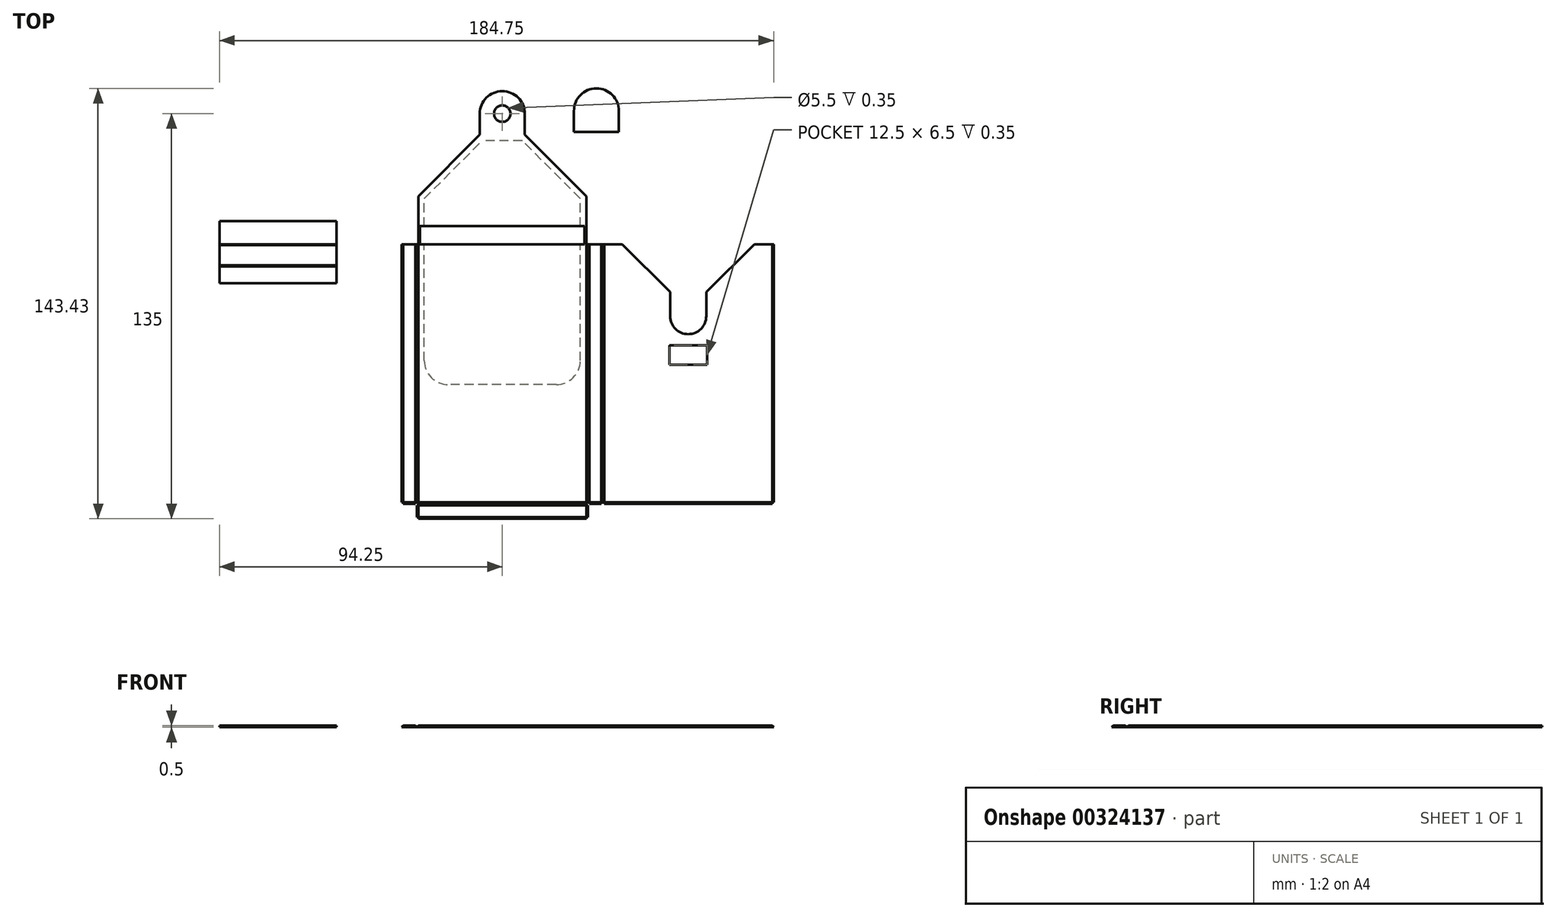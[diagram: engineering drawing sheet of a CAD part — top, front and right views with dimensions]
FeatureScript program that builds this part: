
annotation { "Feature Type Name" : "Feature", "Feature Type Description" : "" }
export const myFeature = defineFeature(function(context is Context, id is Id, definition is map)
    precondition{}
    {
        {
            var Q0;
            Q0=qCreatedBy(makeId("Top.planeOp"),FACE);
            var sketch = newSketch(context, id + "F0", { "sketchPlane" : qUnion([Q0])});
            skLineSegment(sketch, "E0.bottom", {"start": v(0, 0) * mm, "end": v(56, 0) * mm});
            skLineSegment(sketch, "E0.top", {"start": v(0, -86) * mm, "end": v(56, -86) * mm});
            skLineSegment(sketch, "E0.left", {"start": v(0, 0) * mm, "end": v(0, -86) * mm});
            skLineSegment(sketch, "E0.right", {"start": v(56, 0) * mm, "end": v(56, -86) * mm});
            skLineSegment(sketch, "E1.bottom", {"start": v(56, 0) * mm, "end": v(56.5, 0) * mm});
            skLineSegment(sketch, "E1.top", {"start": v(56, -86) * mm, "end": v(56.5, -86) * mm});
            skLineSegment(sketch, "E1.right", {"start": v(56.5, 0) * mm, "end": v(56.5, -86) * mm});
            skLineSegment(sketch, "E2.bottom", {"start": v(56.5, 0) * mm, "end": v(57, 0) * mm});
            skLineSegment(sketch, "E2.top", {"start": v(56.5, -86) * mm, "end": v(57, -86) * mm});
            skLineSegment(sketch, "E2.right", {"start": v(57, 0) * mm, "end": v(57, -86) * mm});
            skLineSegment(sketch, "E3.bottom", {"start": v(57, 0) * mm, "end": v(61, 0) * mm});
            skLineSegment(sketch, "E3.top", {"start": v(57, -86) * mm, "end": v(61, -86) * mm});
            skLineSegment(sketch, "E3.right", {"start": v(61, 0) * mm, "end": v(61, -86) * mm});
            skLineSegment(sketch, "E4.bottom", {"start": v(61, 0) * mm, "end": v(61.5, 0) * mm});
            skLineSegment(sketch, "E4.top", {"start": v(61, -86) * mm, "end": v(61.5, -86) * mm});
            skLineSegment(sketch, "E4.right", {"start": v(61.5, 0) * mm, "end": v(61.5, -86) * mm});
            skLineSegment(sketch, "E5.bottom", {"start": v(61.5, 0) * mm, "end": v(62, 0) * mm});
            skLineSegment(sketch, "E5.top", {"start": v(61.5, -86) * mm, "end": v(62, -86) * mm});
            skLineSegment(sketch, "E5.right", {"start": v(62, 0) * mm, "end": v(62, -86) * mm});
            skLineSegment(sketch, "E6.bottom", {"start": v(62, 0) * mm, "end": v(84, 0) * mm});
            skLineSegment(sketch, "E6.top", {"start": v(62, -86) * mm, "end": v(118, -86) * mm});
            skLineSegment(sketch, "E6.right", {"start": v(118, 0) * mm, "end": v(118, -86) * mm});
            skLineSegment(sketch, "E7", {"start": v(28, 0) * mm, "end": v(28, -86) * mm, "construction": true});
            skLineSegment(sketch, "E8.MirrorCS", {"start": v(-0.5, 0) * mm, "end": v(-0.5, -86) * mm});
            skLineSegment(sketch, "E9.MirrorCS", {"start": v(-1, 0) * mm, "end": v(-1, -86) * mm});
            skLineSegment(sketch, "E10.MirrorCS", {"start": v(-5, 0) * mm, "end": v(-5, -86) * mm});
            skLineSegment(sketch, "E11.MirrorCS", {"start": v(-1, 0) * mm, "end": v(-5, 0) * mm});
            skLineSegment(sketch, "E12.MirrorCS", {"start": v(0, 0) * mm, "end": v(-0.5, 0) * mm});
            skLineSegment(sketch, "E13.MirrorCS", {"start": v(-0.5, 0) * mm, "end": v(-1, 0) * mm});
            skLineSegment(sketch, "E14.MirrorCS", {"start": v(-1, -86) * mm, "end": v(-5, -86) * mm});
            skLineSegment(sketch, "E15.MirrorCS", {"start": v(0, -86) * mm, "end": v(-0.5, -86) * mm});
            skLineSegment(sketch, "E16.MirrorCS", {"start": v(-0.5, -86) * mm, "end": v(-1, -86) * mm});
            skLineSegment(sketch, "E17.MirrorCS", {"start": v(-5.5, 0) * mm, "end": v(-5.5, -86) * mm});
            skLineSegment(sketch, "E18.MirrorCS", {"start": v(-5, 0) * mm, "end": v(-5.5, 0) * mm});
            skLineSegment(sketch, "E19.MirrorCS", {"start": v(-5, -86) * mm, "end": v(-5.5, -86) * mm});
            skLineSegment(sketch, "E20.bottom", {"start": v(118, 0) * mm, "end": v(118.5, 0) * mm});
            skLineSegment(sketch, "E20.top", {"start": v(118, -86) * mm, "end": v(118.5, -86) * mm});
            skLineSegment(sketch, "E20.right", {"start": v(118.5, 0) * mm, "end": v(118.5, -86) * mm});
            skLineSegment(sketch, "E21.top", {"start": v(0, -86.5) * mm, "end": v(56, -86.5) * mm});
            skLineSegment(sketch, "E21.left", {"start": v(0, -86) * mm, "end": v(0, -86.5) * mm});
            skLineSegment(sketch, "E21.right", {"start": v(56, -86) * mm, "end": v(56, -86.5) * mm});
            skLineSegment(sketch, "E22.bottom", {"start": v(56, -86.5) * mm, "end": v(0, -86.5) * mm});
            skLineSegment(sketch, "E22.top", {"start": v(56, -87) * mm, "end": v(0, -87) * mm});
            skLineSegment(sketch, "E22.left", {"start": v(56, -86.5) * mm, "end": v(56, -87) * mm});
            skLineSegment(sketch, "E22.right", {"start": v(0, -86.5) * mm, "end": v(0, -87) * mm});
            skLineSegment(sketch, "E23.bottom", {"start": v(0, -87) * mm, "end": v(56, -87) * mm});
            skLineSegment(sketch, "E23.top", {"start": v(0, -91) * mm, "end": v(56, -91) * mm});
            skLineSegment(sketch, "E23.left", {"start": v(0, -87) * mm, "end": v(0, -91) * mm});
            skLineSegment(sketch, "E23.right", {"start": v(56, -87) * mm, "end": v(56, -91) * mm});
            skLineSegment(sketch, "E24.bottom", {"start": v(56, -91) * mm, "end": v(0, -91) * mm});
            skLineSegment(sketch, "E24.top", {"start": v(56, -91.5) * mm, "end": v(0, -91.5) * mm});
            skLineSegment(sketch, "E24.left", {"start": v(56, -91) * mm, "end": v(56, -91.5) * mm});
            skLineSegment(sketch, "E24.right", {"start": v(0, -91) * mm, "end": v(0, -91.5) * mm});
            skLineSegment(sketch, "E25.bottom", {"start": v(-5, -86) * mm, "end": v(-1, -86) * mm});
            skLineSegment(sketch, "E25.top", {"start": v(-5, -86.5) * mm, "end": v(-1, -86.5) * mm});
            skLineSegment(sketch, "E25.left", {"start": v(-5, -86) * mm, "end": v(-5, -86.5) * mm});
            skLineSegment(sketch, "E25.right", {"start": v(-1, -86) * mm, "end": v(-1, -86.5) * mm});
            skLineSegment(sketch, "E26.bottom", {"start": v(0, -87) * mm, "end": v(-0.5, -87) * mm});
            skLineSegment(sketch, "E26.top", {"start": v(0, -91) * mm, "end": v(-0.5, -91) * mm});
            skLineSegment(sketch, "E26.right", {"start": v(-0.5, -87) * mm, "end": v(-0.5, -91) * mm});
            skLineSegment(sketch, "E27.bottom", {"start": v(56, -87) * mm, "end": v(56.5, -87) * mm});
            skLineSegment(sketch, "E27.top", {"start": v(56, -91) * mm, "end": v(56.5, -91) * mm});
            skLineSegment(sketch, "E27.right", {"start": v(56.5, -87) * mm, "end": v(56.5, -91) * mm});
            skLineSegment(sketch, "E28.top", {"start": v(57, -86.5) * mm, "end": v(61, -86.5) * mm});
            skLineSegment(sketch, "E28.left", {"start": v(57, -86) * mm, "end": v(57, -86.5) * mm});
            skLineSegment(sketch, "E28.right", {"start": v(61, -86) * mm, "end": v(61, -86.5) * mm});
            skLineSegment(sketch, "E29.top", {"start": v(62, -86.5) * mm, "end": v(118, -86.5) * mm});
            skLineSegment(sketch, "E29.left", {"start": v(62, -86) * mm, "end": v(62, -86.5) * mm});
            skLineSegment(sketch, "E29.right", {"start": v(118, -86) * mm, "end": v(118, -86.5) * mm});
            skLineSegment(sketch, "E30.top", {"start": v(0, 8) * mm, "end": v(56, 8) * mm});
            skLineSegment(sketch, "E30.left", {"start": v(0, 0) * mm, "end": v(0, 8) * mm});
            skLineSegment(sketch, "E30.right", {"start": v(56, 0) * mm, "end": v(56, 8) * mm});
            skLineSegment(sketch, "E31.top", {"start": v(0, 51) * mm, "end": v(56, 51) * mm});
            skLineSegment(sketch, "E31.left", {"start": v(0, 8) * mm, "end": v(0, 51) * mm});
            skLineSegment(sketch, "E31.right", {"start": v(56, 8) * mm, "end": v(56, 51) * mm});
            skPoint(sketch, "E32.visualSharp", {"position": v(0, 51) * mm});
            skLineSegment(sketch, "E32.filletArc", {"start": v(0, 51) * mm, "end": v(0, 51) * mm});
            skPoint(sketch, "E33.visualSharp", {"position": v(56, 51) * mm});
            skLineSegment(sketch, "E33.filletArc", {"start": v(56, 51) * mm, "end": v(56, 51) * mm});
            skLineSegment(sketch, "E34.top", {"start": v(96, -30) * mm, "end": v(84, -30) * mm});
            skLineSegment(sketch, "E34.left", {"start": v(96, 0) * mm, "end": v(96, -30) * mm});
            skLineSegment(sketch, "E34.right", {"start": v(84, 0) * mm, "end": v(84, -30) * mm});
            skPoint(sketch, "E34.middle", {"position": v(90, -15) * mm});
            skPoint(sketch, "E34.middle.positionSnap0", {"position": v(90, 0) * mm});
            skPoint(sketch, "E34.centerSnap0", {"position": v(90, 0) * mm});
            skLineSegment(sketch, "E35.trimOffspring", {"start": v(96, 0) * mm, "end": v(118, 0) * mm});
            skSolve(sketch);
        }
        {
            var Q0;
            Q0 = qSketchRegion(id + "F0", true);
            extrude(context, id + "F1", {"entities" : qUnion([Q0]), "depth" : 0.5 * mm});
        }
        {
            var Q0;
            Q0=makeQuery(id+"F1.opExtrude","CAP_EDGE",EDGE,{"disambiguationData":[OSD([sQuery(id+"F0.wireOp",EDGE,"E17.MirrorCS")])],"isStart":false});
            var Q1;
            Q1=makeQuery(id+"F1.opExtrude","CAP_EDGE",EDGE,{"disambiguationData":[OSD([sQuery(id+"F0.wireOp",EDGE,"E25.top")])],"isStart":false});
            var Q2;
            Q2=makeQuery(id+"F1.opExtrude","CAP_EDGE",EDGE,{"disambiguationData":[OSD([sQuery(id+"F0.wireOp",EDGE,"E26.right")])],"isStart":false});
            var Q3;
            Q3=makeQuery(id+"F1.opExtrude","CAP_EDGE",EDGE,{"disambiguationData":[OSD([sQuery(id+"F0.wireOp",EDGE,"E24.top")])],"isStart":false});
            var Q4;
            Q4=makeQuery(id+"F1.opExtrude","CAP_EDGE",EDGE,{"disambiguationData":[OSD([sQuery(id+"F0.wireOp",EDGE,"E27.right")])],"isStart":false});
            var Q5;
            Q5=makeQuery(id+"F1.opExtrude","CAP_EDGE",EDGE,{"disambiguationData":[OSD([sQuery(id+"F0.wireOp",EDGE,"E28.top")])],"isStart":false});
            var Q6;
            Q6=makeQuery(id+"F1.opExtrude","CAP_EDGE",EDGE,{"disambiguationData":[OSD([sQuery(id+"F0.wireOp",EDGE,"E29.top")])],"isStart":false});
            var Q7;
            Q7=makeQuery(id+"F1.opExtrude","CAP_EDGE",EDGE,{"disambiguationData":[OSD([sQuery(id+"F0.wireOp",EDGE,"E20.right")])],"isStart":false});
            chamfer(context, id + "F2", {"entities" : qUnion([Q0, Q1, Q2, Q3, Q4, Q5, Q6, Q7]), "chamferType" : ChamferType.OFFSET_ANGLE, "width" : 0.5 * mm, "oppositeDirection" : false, "angle" : 45 * degree, "tangentPropagation" : true});
        }
        {
            var Q0;
            Q0=makeQuery(id+"F1.opExtrude","SWEPT_FACE",FACE,{"disambiguationData":[OSD([sQuery(id+"F0.wireOp",EDGE,"E15.MirrorCS"),sQuery(id+"F0.wireOp",EDGE,"E16.MirrorCS")])]});
            var sketch = newSketch(context, id + "F3", { "sketchPlane" : qUnion([Q0])});
            skLineSegment(sketch, "E36", {"start": v(-1, 0.5) * mm, "end": v(0, 0.5) * mm});
            skLineSegment(sketch, "E37", {"start": v(0, 0.5) * mm, "end": v(-0.35, 0.15) * mm});
            skLineSegment(sketch, "E38", {"start": v(-0.35, 0.15) * mm, "end": v(-0.65, 0.15) * mm});
            skLineSegment(sketch, "E39", {"start": v(-0.65, 0.15) * mm, "end": v(-1, 0.5) * mm});
            skLineSegment(sketch, "E40", {"start": v(56, 0.5) * mm, "end": v(57, 0.5) * mm});
            skLineSegment(sketch, "E41", {"start": v(57, 0.5) * mm, "end": v(56.65, 0.15) * mm});
            skLineSegment(sketch, "E42", {"start": v(56.65, 0.15) * mm, "end": v(56.35, 0.15) * mm});
            skLineSegment(sketch, "E43", {"start": v(56.35, 0.15) * mm, "end": v(56, 0.5) * mm});
            skLineSegment(sketch, "E44", {"start": v(61, 0.5) * mm, "end": v(62, 0.5) * mm});
            skLineSegment(sketch, "E45", {"start": v(62, 0.5) * mm, "end": v(61.65, 0.15) * mm});
            skLineSegment(sketch, "E46", {"start": v(61.65, 0.15) * mm, "end": v(61.35, 0.15) * mm});
            skLineSegment(sketch, "E47", {"start": v(61.35, 0.15) * mm, "end": v(61, 0.5) * mm});
            skSolve(sketch);
        }
        {
            var Q0;
            Q0 = qSketchRegion(id + "F3", true);
            extrude(context, id + "F4", {"entities" : qUnion([Q0]), "operationType" : NewBodyOperationType.REMOVE, "endBound" : BoundingType.UP_TO_NEXT, "oppositeDirection" : true, "depth" : 25 * mm});
        }
        {
            var Q0;
            {var subQ0=sQuery(id+"F0.wireOp",EDGE,"E26.top");var subQ1=sQuery(id+"F0.wireOp",EDGE,"E26.bottom");var subQ2=sQuery(id+"F0.wireOp",EDGE,"E24.left");var subQ3=sQuery(id+"F0.wireOp",EDGE,"E22.right");var subQ4=sQuery(id+"F0.wireOp",EDGE,"E21.left");var subQ5=sQuery(id+"F0.wireOp",EDGE,"E22.left");var subQ6=sQuery(id+"F0.wireOp",EDGE,"E21.right");var subQ7=sQuery(id+"F0.wireOp",EDGE,"E26.right");var subQ8=sQuery(id+"F0.wireOp",EDGE,"E6.bottom");var subQ9=sQuery(id+"F0.wireOp",EDGE,"E5.bottom");var subQ10=sQuery(id+"F0.wireOp",EDGE,"E4.bottom");var subQ11=sQuery(id+"F0.wireOp",EDGE,"E3.bottom");var subQ12=sQuery(id+"F0.wireOp",EDGE,"E2.bottom");var subQ13=sQuery(id+"F0.wireOp",EDGE,"E1.bottom");var subQ14=sQuery(id+"F0.wireOp",EDGE,"E2.top");var subQ15=sQuery(id+"F0.wireOp",EDGE,"E1.top");var subQ16=sQuery(id+"F0.wireOp",EDGE,"E24.right");var subQ17=sQuery(id+"F0.wireOp",EDGE,"E18.MirrorCS");var subQ18=sQuery(id+"F0.wireOp",EDGE,"E13.MirrorCS");var subQ19=sQuery(id+"F0.wireOp",EDGE,"E12.MirrorCS");var subQ20=sQuery(id+"F0.wireOp",EDGE,"E11.MirrorCS");var subQ21=sQuery(id+"F0.wireOp",EDGE,"E16.MirrorCS");var subQ22=sQuery(id+"F0.wireOp",EDGE,"E15.MirrorCS");var subQ23=sQuery(id+"F0.wireOp",EDGE,"E27.bottom");var subQ24=sQuery(id+"F0.wireOp",EDGE,"E27.top");var subQ25=sQuery(id+"F0.wireOp",EDGE,"E31.left");var subQ26=sQuery(id+"F0.wireOp",EDGE,"E30.left");var subQ27=sQuery(id+"F0.wireOp",EDGE,"E31.right");var subQ28=sQuery(id+"F0.wireOp",EDGE,"E30.right");var subQ29=sQuery(id+"F0.wireOp",EDGE,"E31.top");var subQ30=sQuery(id+"F0.wireOp",EDGE,"E24.top");var subQ31=sQuery(id+"F0.wireOp",EDGE,"E27.right");Q0=makeQuery(id+"F4.boolean.opBoolean","SPLIT",FACE,{"disambiguationData":[TD([makeQuery(id+"F1.opExtrude","SWEPT_FACE",FACE,{"disambiguationData":[OSD([subQ2])]})])],"derivedFrom":makeQuery(id+"F1.opExtrude","CAP_FACE",FACE,{"disambiguationData":[OSD([subQ13,subQ15,subQ12,subQ14,subQ11,subQ10,sQuery(id+"F0.wireOp",EDGE,"E4.top"),subQ9,sQuery(id+"F0.wireOp",EDGE,"E5.top"),subQ8,subQ20,subQ19,subQ18,subQ22,subQ21,sQuery(id+"F0.wireOp",EDGE,"E17.MirrorCS"),subQ17,sQuery(id+"F0.wireOp",EDGE,"E19.MirrorCS"),sQuery(id+"F0.wireOp",EDGE,"E20.bottom"),sQuery(id+"F0.wireOp",EDGE,"E20.top"),sQuery(id+"F0.wireOp",EDGE,"E20.right"),subQ4,subQ6,subQ5,subQ3,subQ30,subQ2,subQ16,sQuery(id+"F0.wireOp",EDGE,"E25.top"),sQuery(id+"F0.wireOp",EDGE,"E25.left"),sQuery(id+"F0.wireOp",EDGE,"E25.right"),subQ1,subQ0,subQ7,subQ23,subQ24,subQ31,sQuery(id+"F0.wireOp",EDGE,"E28.top"),sQuery(id+"F0.wireOp",EDGE,"E28.left"),sQuery(id+"F0.wireOp",EDGE,"E28.right"),sQuery(id+"F0.wireOp",EDGE,"E29.top"),sQuery(id+"F0.wireOp",EDGE,"E29.left"),sQuery(id+"F0.wireOp",EDGE,"E29.right"),subQ26,subQ28,subQ29,subQ25,subQ27,sQuery(id+"F0.wireOp",EDGE,"E34.top"),sQuery(id+"F0.wireOp",EDGE,"E34.left"),sQuery(id+"F0.wireOp",EDGE,"E34.right"),sQuery(id+"F0.wireOp",EDGE,"E35.trimOffspring")])],"isStart":false})});}
            var sketch = newSketch(context, id + "F5", { "sketchPlane" : qUnion([Q0])});
            skLineSegment(sketch, "E48", {"start": v(28, 51) * mm, "end": v(28, 0) * mm, "construction": true});
            skLineSegment(sketch, "E49", {"start": v(22, 51) * mm, "end": v(28, 51) * mm});
            skLineSegment(sketch, "E50", {"start": v(20.5, 43.5) * mm, "end": v(20.5, 36.5) * mm});
            skLineSegment(sketch, "E51", {"start": v(20.5, 36.5) * mm, "end": v(0, 16) * mm});
            skLineSegment(sketch, "E52", {"start": v(0, 16) * mm, "end": v(0, 51) * mm});
            skLineSegment(sketch, "E53", {"start": v(0, 51) * mm, "end": v(22, 51) * mm});
            skLineSegment(sketch, "E54.MirrorCS", {"start": v(56, 51) * mm, "end": v(34, 51) * mm});
            skLineSegment(sketch, "E55.MirrorCS", {"start": v(35.5, 43.5) * mm, "end": v(35.5, 36.5) * mm});
            skLineSegment(sketch, "E56.MirrorCS", {"start": v(35.5, 36.5) * mm, "end": v(56, 16) * mm});
            skLineSegment(sketch, "E57.MirrorCS", {"start": v(56, 16) * mm, "end": v(56, 51) * mm});
            skArc(sketch, "E58", {"start": v(35.5, 43.5) * mm, "mid": v(28, 51) * mm, "end": v(20.5, 43.5) * mm});
            skLineSegment(sketch, "E59", {"start": v(28, 51) * mm, "end": v(34, 51) * mm});
            skSolve(sketch);
        }
        {
            var Q0;
            Q0 = qSketchRegion(id + "F5", true);
            extrude(context, id + "F6", {"entities" : qUnion([Q0]), "operationType" : NewBodyOperationType.REMOVE, "oppositeDirection" : true, "depth" : 25 * mm});
        }
        {
            var Q0;
            {var subQ0=sQuery(id+"F0.wireOp",EDGE,"E26.top");var subQ1=sQuery(id+"F0.wireOp",EDGE,"E26.bottom");var subQ2=sQuery(id+"F0.wireOp",EDGE,"E24.left");var subQ3=sQuery(id+"F0.wireOp",EDGE,"E22.right");var subQ4=sQuery(id+"F0.wireOp",EDGE,"E21.left");var subQ5=sQuery(id+"F0.wireOp",EDGE,"E22.left");var subQ6=sQuery(id+"F0.wireOp",EDGE,"E21.right");var subQ7=sQuery(id+"F0.wireOp",EDGE,"E26.right");var subQ8=sQuery(id+"F0.wireOp",EDGE,"E6.bottom");var subQ9=sQuery(id+"F0.wireOp",EDGE,"E5.bottom");var subQ10=sQuery(id+"F0.wireOp",EDGE,"E4.bottom");var subQ11=sQuery(id+"F0.wireOp",EDGE,"E3.bottom");var subQ12=sQuery(id+"F0.wireOp",EDGE,"E2.bottom");var subQ13=sQuery(id+"F0.wireOp",EDGE,"E1.bottom");var subQ14=sQuery(id+"F0.wireOp",EDGE,"E2.top");var subQ15=sQuery(id+"F0.wireOp",EDGE,"E1.top");var subQ16=sQuery(id+"F0.wireOp",EDGE,"E24.right");var subQ17=sQuery(id+"F0.wireOp",EDGE,"E18.MirrorCS");var subQ18=sQuery(id+"F0.wireOp",EDGE,"E13.MirrorCS");var subQ19=sQuery(id+"F0.wireOp",EDGE,"E12.MirrorCS");var subQ20=sQuery(id+"F0.wireOp",EDGE,"E11.MirrorCS");var subQ21=sQuery(id+"F0.wireOp",EDGE,"E16.MirrorCS");var subQ22=sQuery(id+"F0.wireOp",EDGE,"E15.MirrorCS");var subQ23=sQuery(id+"F0.wireOp",EDGE,"E27.bottom");var subQ24=sQuery(id+"F0.wireOp",EDGE,"E27.top");var subQ25=sQuery(id+"F0.wireOp",EDGE,"E31.left");var subQ26=sQuery(id+"F0.wireOp",EDGE,"E30.left");var subQ27=sQuery(id+"F0.wireOp",EDGE,"E31.right");var subQ28=sQuery(id+"F0.wireOp",EDGE,"E30.right");var subQ29=sQuery(id+"F0.wireOp",EDGE,"E31.top");var subQ30=sQuery(id+"F0.wireOp",EDGE,"E24.top");var subQ31=sQuery(id+"F0.wireOp",EDGE,"E27.right");Q0=makeQuery(id+"F4.boolean.opBoolean","SPLIT",FACE,{"disambiguationData":[TD([makeQuery(id+"F1.opExtrude","SWEPT_FACE",FACE,{"disambiguationData":[OSD([subQ2])]})])],"derivedFrom":makeQuery(id+"F1.opExtrude","CAP_FACE",FACE,{"disambiguationData":[OSD([subQ13,subQ15,subQ12,subQ14,subQ11,subQ10,sQuery(id+"F0.wireOp",EDGE,"E4.top"),subQ9,sQuery(id+"F0.wireOp",EDGE,"E5.top"),subQ8,subQ20,subQ19,subQ18,subQ22,subQ21,sQuery(id+"F0.wireOp",EDGE,"E17.MirrorCS"),subQ17,sQuery(id+"F0.wireOp",EDGE,"E19.MirrorCS"),sQuery(id+"F0.wireOp",EDGE,"E20.bottom"),sQuery(id+"F0.wireOp",EDGE,"E20.top"),sQuery(id+"F0.wireOp",EDGE,"E20.right"),subQ4,subQ6,subQ5,subQ3,subQ30,subQ2,subQ16,sQuery(id+"F0.wireOp",EDGE,"E25.top"),sQuery(id+"F0.wireOp",EDGE,"E25.left"),sQuery(id+"F0.wireOp",EDGE,"E25.right"),subQ1,subQ0,subQ7,subQ23,subQ24,subQ31,sQuery(id+"F0.wireOp",EDGE,"E28.top"),sQuery(id+"F0.wireOp",EDGE,"E28.left"),sQuery(id+"F0.wireOp",EDGE,"E28.right"),sQuery(id+"F0.wireOp",EDGE,"E29.top"),sQuery(id+"F0.wireOp",EDGE,"E29.left"),sQuery(id+"F0.wireOp",EDGE,"E29.right"),subQ26,subQ28,subQ29,subQ25,subQ27,sQuery(id+"F0.wireOp",EDGE,"E34.top"),sQuery(id+"F0.wireOp",EDGE,"E34.left"),sQuery(id+"F0.wireOp",EDGE,"E34.right"),sQuery(id+"F0.wireOp",EDGE,"E35.trimOffspring")])],"isStart":false})});}
            var sketch = newSketch(context, id + "F7", { "sketchPlane" : qUnion([Q0])});
            skCircle(sketch, "E60", {"center": v(28, 43.5) * mm, "radius": 2.75 * mm});
            skPoint(sketch, "E60.centerSnap0", {"position": v(28, 54) * mm});
            skSolve(sketch);
        }
        {
            var Q0;
            Q0 = qSketchRegion(id + "F7", true);
            extrude(context, id + "F8", {"entities" : qUnion([Q0]), "operationType" : NewBodyOperationType.REMOVE, "oppositeDirection" : true, "depth" : 0.35 * mm});
        }
        {
            var Q0;
            {var subQ0=sQuery(id+"F0.wireOp",EDGE,"E20.right");var subQ1=sQuery(id+"F0.wireOp",EDGE,"E20.top");var subQ2=sQuery(id+"F0.wireOp",EDGE,"E34.left");var subQ3=sQuery(id+"F0.wireOp",EDGE,"E29.left");var subQ4=sQuery(id+"F0.wireOp",EDGE,"E34.top");var subQ5=sQuery(id+"F0.wireOp",EDGE,"E6.bottom");var subQ6=sQuery(id+"F0.wireOp",EDGE,"E5.bottom");var subQ7=sQuery(id+"F0.wireOp",EDGE,"E4.bottom");var subQ8=sQuery(id+"F0.wireOp",EDGE,"E3.bottom");var subQ9=sQuery(id+"F0.wireOp",EDGE,"E2.bottom");var subQ10=sQuery(id+"F0.wireOp",EDGE,"E1.bottom");var subQ11=sQuery(id+"F0.wireOp",EDGE,"E34.right");var subQ12=sQuery(id+"F0.wireOp",EDGE,"E5.top");var subQ13=sQuery(id+"F0.wireOp",EDGE,"E4.top");var subQ14=sQuery(id+"F0.wireOp",EDGE,"E29.right");var subQ15=sQuery(id+"F0.wireOp",EDGE,"E35.trimOffspring");var subQ16=sQuery(id+"F0.wireOp",EDGE,"E20.bottom");var subQ17=sQuery(id+"F0.wireOp",EDGE,"E29.top");Q0=makeQuery(id+"F4.boolean.opBoolean","SPLIT",FACE,{"disambiguationData":[TD([makeQuery(id+"F1.opExtrude","SWEPT_FACE",FACE,{"disambiguationData":[OSD([subQ1])]})])],"derivedFrom":makeQuery(id+"F1.opExtrude","CAP_FACE",FACE,{"disambiguationData":[OSD([subQ10,sQuery(id+"F0.wireOp",EDGE,"E1.top"),subQ9,sQuery(id+"F0.wireOp",EDGE,"E2.top"),subQ8,subQ7,subQ13,subQ6,subQ12,subQ5,sQuery(id+"F0.wireOp",EDGE,"E11.MirrorCS"),sQuery(id+"F0.wireOp",EDGE,"E12.MirrorCS"),sQuery(id+"F0.wireOp",EDGE,"E13.MirrorCS"),sQuery(id+"F0.wireOp",EDGE,"E15.MirrorCS"),sQuery(id+"F0.wireOp",EDGE,"E16.MirrorCS"),sQuery(id+"F0.wireOp",EDGE,"E17.MirrorCS"),sQuery(id+"F0.wireOp",EDGE,"E18.MirrorCS"),sQuery(id+"F0.wireOp",EDGE,"E19.MirrorCS"),subQ16,subQ1,subQ0,sQuery(id+"F0.wireOp",EDGE,"E21.left"),sQuery(id+"F0.wireOp",EDGE,"E21.right"),sQuery(id+"F0.wireOp",EDGE,"E22.left"),sQuery(id+"F0.wireOp",EDGE,"E22.right"),sQuery(id+"F0.wireOp",EDGE,"E24.top"),sQuery(id+"F0.wireOp",EDGE,"E24.left"),sQuery(id+"F0.wireOp",EDGE,"E24.right"),sQuery(id+"F0.wireOp",EDGE,"E25.top"),sQuery(id+"F0.wireOp",EDGE,"E25.left"),sQuery(id+"F0.wireOp",EDGE,"E25.right"),sQuery(id+"F0.wireOp",EDGE,"E26.bottom"),sQuery(id+"F0.wireOp",EDGE,"E26.top"),sQuery(id+"F0.wireOp",EDGE,"E26.right"),sQuery(id+"F0.wireOp",EDGE,"E27.bottom"),sQuery(id+"F0.wireOp",EDGE,"E27.top"),sQuery(id+"F0.wireOp",EDGE,"E27.right"),sQuery(id+"F0.wireOp",EDGE,"E28.top"),sQuery(id+"F0.wireOp",EDGE,"E28.left"),sQuery(id+"F0.wireOp",EDGE,"E28.right"),subQ17,subQ3,subQ14,sQuery(id+"F0.wireOp",EDGE,"E30.left"),sQuery(id+"F0.wireOp",EDGE,"E30.right"),sQuery(id+"F0.wireOp",EDGE,"E31.top"),sQuery(id+"F0.wireOp",EDGE,"E31.left"),sQuery(id+"F0.wireOp",EDGE,"E31.right"),subQ4,subQ2,subQ11,subQ15])],"isStart":false})});}
            var sketch = newSketch(context, id + "F9", { "sketchPlane" : qUnion([Q0])});
            skLineSegment(sketch, "E61.bottom", {"start": v(83.75, -33.75) * mm, "end": v(96.25, -33.75) * mm});
            skLineSegment(sketch, "E61.top", {"start": v(83.75, -40.25) * mm, "end": v(96.25, -40.25) * mm});
            skLineSegment(sketch, "E61.left", {"start": v(83.75, -33.75) * mm, "end": v(83.75, -40.25) * mm});
            skLineSegment(sketch, "E61.right", {"start": v(96.25, -33.75) * mm, "end": v(96.25, -40.25) * mm});
            skPoint(sketch, "E61.middle", {"position": v(90, -37) * mm});
            skPoint(sketch, "E61.middle.positionSnap0", {"position": v(90, -30) * mm});
            skPoint(sketch, "E61.centerSnap0", {"position": v(90, -30) * mm});
            skSolve(sketch);
        }
        {
            var Q0;
            Q0 = qSketchRegion(id + "F9", true);
            extrude(context, id + "F10", {"entities" : qUnion([Q0]), "operationType" : NewBodyOperationType.REMOVE, "oppositeDirection" : true, "depth" : 0.35 * mm});
        }
        {
            var Q0;
            Q0=qCreatedBy(makeId("Top.planeOp"),FACE);
            var sketch = newSketch(context, id + "F11", { "sketchPlane" : qUnion([Q0])});
            skLineSegment(sketch, "E62.bottom", {"start": v(-66.25, 0) * mm, "end": v(-27.2, 0) * mm});
            skLineSegment(sketch, "E62.top", {"start": v(-66.25, -7.37) * mm, "end": v(-27.2, -7.37) * mm});
            skLineSegment(sketch, "E62.left", {"start": v(-66.25, 0) * mm, "end": v(-66.25, -7.37) * mm});
            skLineSegment(sketch, "E62.right", {"start": v(-27.2, 0) * mm, "end": v(-27.2, -7.37) * mm});
            skLineSegment(sketch, "E63.top", {"start": v(-66.25, -13.07) * mm, "end": v(-27.2, -13.07) * mm});
            skLineSegment(sketch, "E63.left", {"start": v(-66.25, -7.37) * mm, "end": v(-66.25, -13.07) * mm});
            skLineSegment(sketch, "E63.right", {"start": v(-27.2, -7.37) * mm, "end": v(-27.2, -13.07) * mm});
            skLineSegment(sketch, "E64.top", {"start": v(-66.25, 7.64) * mm, "end": v(-27.2, 7.64) * mm});
            skLineSegment(sketch, "E64.left", {"start": v(-66.25, 0) * mm, "end": v(-66.25, 7.64) * mm});
            skLineSegment(sketch, "E64.right", {"start": v(-27.2, 0) * mm, "end": v(-27.2, 7.64) * mm});
            skSolve(sketch);
        }
        {
            var Q0;
            Q0=makeQuery(id+"F11.imprint","IMPRINT",FACE,{"disambiguationData":[TD([[makeQuery(id+"F11.imprint","IMPRINT",EDGE,{"derivedFrom":sQuery(id+"F11.wireOp",EDGE,"E62.top")}),-1.0]])]});
            var Q1;
            Q1=makeQuery(id+"F11.imprint","IMPRINT",FACE,{"disambiguationData":[TD([[makeQuery(id+"F11.imprint","IMPRINT",EDGE,{"derivedFrom":sQuery(id+"F11.wireOp",EDGE,"E62.bottom")}),1.0]])]});
            var Q2;
            Q2=makeQuery(id+"F11.imprint","IMPRINT",FACE,{"disambiguationData":[TD([[makeQuery(id+"F11.imprint","IMPRINT",EDGE,{"derivedFrom":sQuery(id+"F11.wireOp",EDGE,"E62.left")}),1.0]])]});
            extrude(context, id + "F12", {"entities" : qUnion([Q0, Q1, Q2]), "depth" : 0.15 * mm});
        }
        {
            var Q0;
            Q0=makeQuery(id+"F11.imprint","IMPRINT",FACE,{"disambiguationData":[TD([[makeQuery(id+"F11.imprint","IMPRINT",EDGE,{"derivedFrom":sQuery(id+"F11.wireOp",EDGE,"E62.top")}),-1.0]])]});
            var Q1;
            Q1=makeQuery(id+"F11.imprint","IMPRINT",FACE,{"disambiguationData":[TD([[makeQuery(id+"F11.imprint","IMPRINT",EDGE,{"derivedFrom":sQuery(id+"F11.wireOp",EDGE,"E62.bottom")}),1.0]])]});
            extrude(context, id + "F13", {"entities" : qUnion([Q0, Q1]), "operationType" : NewBodyOperationType.ADD, "depth" : 0.5 * mm});
        }
        {
            var Q0;
            Q0=makeQuery(id+"F13.boolean.opBoolean","INTERSECT",EDGE,{"derivedFrom":[makeQuery(id+"F12.opExtrude","CAP_FACE",FACE,{"disambiguationData":[OSD([sQuery(id+"F11.wireOp",EDGE,"E62.left"),sQuery(id+"F11.wireOp",EDGE,"E62.right"),sQuery(id+"F11.wireOp",EDGE,"E63.top"),sQuery(id+"F11.wireOp",EDGE,"E63.left"),sQuery(id+"F11.wireOp",EDGE,"E63.right"),sQuery(id+"F11.wireOp",EDGE,"E64.top"),sQuery(id+"F11.wireOp",EDGE,"E64.left"),sQuery(id+"F11.wireOp",EDGE,"E64.right")])],"isStart":false}),makeQuery(id+"F13.opExtrude","SWEPT_FACE",FACE,{"disambiguationData":[OSD([sQuery(id+"F11.wireOp",EDGE,"E62.top")])]})]});
            var Q1;
            Q1=makeQuery(id+"F13.boolean.opBoolean","INTERSECT",EDGE,{"derivedFrom":[makeQuery(id+"F12.opExtrude","CAP_FACE",FACE,{"disambiguationData":[OSD([sQuery(id+"F11.wireOp",EDGE,"E62.left"),sQuery(id+"F11.wireOp",EDGE,"E62.right"),sQuery(id+"F11.wireOp",EDGE,"E63.top"),sQuery(id+"F11.wireOp",EDGE,"E63.left"),sQuery(id+"F11.wireOp",EDGE,"E63.right"),sQuery(id+"F11.wireOp",EDGE,"E64.top"),sQuery(id+"F11.wireOp",EDGE,"E64.left"),sQuery(id+"F11.wireOp",EDGE,"E64.right")])],"isStart":false}),makeQuery(id+"F13.opExtrude","SWEPT_FACE",FACE,{"disambiguationData":[OSD([sQuery(id+"F11.wireOp",EDGE,"E62.bottom")])]})]});
            chamfer(context, id + "F14", {"entities" : qUnion([Q0, Q1]), "width" : 0.35 * mm, "tangentPropagation" : true});
        }
        {
            var Q0;
            {var subQ0=sQuery(id+"F0.wireOp",EDGE,"E26.top");var subQ1=sQuery(id+"F0.wireOp",EDGE,"E26.bottom");var subQ2=sQuery(id+"F0.wireOp",EDGE,"E24.left");var subQ3=sQuery(id+"F0.wireOp",EDGE,"E22.right");var subQ4=sQuery(id+"F0.wireOp",EDGE,"E21.left");var subQ5=sQuery(id+"F0.wireOp",EDGE,"E22.left");var subQ6=sQuery(id+"F0.wireOp",EDGE,"E21.right");var subQ7=sQuery(id+"F0.wireOp",EDGE,"E26.right");var subQ8=sQuery(id+"F0.wireOp",EDGE,"E6.bottom");var subQ9=sQuery(id+"F0.wireOp",EDGE,"E5.bottom");var subQ10=sQuery(id+"F0.wireOp",EDGE,"E4.bottom");var subQ11=sQuery(id+"F0.wireOp",EDGE,"E3.bottom");var subQ12=sQuery(id+"F0.wireOp",EDGE,"E2.bottom");var subQ13=sQuery(id+"F0.wireOp",EDGE,"E1.bottom");var subQ14=sQuery(id+"F0.wireOp",EDGE,"E2.top");var subQ15=sQuery(id+"F0.wireOp",EDGE,"E1.top");var subQ16=sQuery(id+"F0.wireOp",EDGE,"E24.right");var subQ17=sQuery(id+"F0.wireOp",EDGE,"E18.MirrorCS");var subQ18=sQuery(id+"F0.wireOp",EDGE,"E13.MirrorCS");var subQ19=sQuery(id+"F0.wireOp",EDGE,"E12.MirrorCS");var subQ20=sQuery(id+"F0.wireOp",EDGE,"E11.MirrorCS");var subQ21=sQuery(id+"F0.wireOp",EDGE,"E16.MirrorCS");var subQ22=sQuery(id+"F0.wireOp",EDGE,"E15.MirrorCS");var subQ23=sQuery(id+"F0.wireOp",EDGE,"E27.bottom");var subQ24=sQuery(id+"F0.wireOp",EDGE,"E27.top");var subQ25=sQuery(id+"F0.wireOp",EDGE,"E31.left");var subQ26=sQuery(id+"F0.wireOp",EDGE,"E30.left");var subQ27=sQuery(id+"F0.wireOp",EDGE,"E31.right");var subQ28=sQuery(id+"F0.wireOp",EDGE,"E30.right");var subQ29=sQuery(id+"F0.wireOp",EDGE,"E31.top");var subQ30=sQuery(id+"F0.wireOp",EDGE,"E24.top");var subQ31=sQuery(id+"F0.wireOp",EDGE,"E27.right");Q0=makeQuery(id+"F4.boolean.opBoolean","SPLIT",FACE,{"disambiguationData":[TD([makeQuery(id+"F1.opExtrude","SWEPT_FACE",FACE,{"disambiguationData":[OSD([subQ2])]})])],"derivedFrom":makeQuery(id+"F1.opExtrude","CAP_FACE",FACE,{"disambiguationData":[OSD([subQ13,subQ15,subQ12,subQ14,subQ11,subQ10,sQuery(id+"F0.wireOp",EDGE,"E4.top"),subQ9,sQuery(id+"F0.wireOp",EDGE,"E5.top"),subQ8,subQ20,subQ19,subQ18,subQ22,subQ21,sQuery(id+"F0.wireOp",EDGE,"E17.MirrorCS"),subQ17,sQuery(id+"F0.wireOp",EDGE,"E19.MirrorCS"),sQuery(id+"F0.wireOp",EDGE,"E20.bottom"),sQuery(id+"F0.wireOp",EDGE,"E20.top"),sQuery(id+"F0.wireOp",EDGE,"E20.right"),subQ4,subQ6,subQ5,subQ3,subQ30,subQ2,subQ16,sQuery(id+"F0.wireOp",EDGE,"E25.top"),sQuery(id+"F0.wireOp",EDGE,"E25.left"),sQuery(id+"F0.wireOp",EDGE,"E25.right"),subQ1,subQ0,subQ7,subQ23,subQ24,subQ31,sQuery(id+"F0.wireOp",EDGE,"E28.top"),sQuery(id+"F0.wireOp",EDGE,"E28.left"),sQuery(id+"F0.wireOp",EDGE,"E28.right"),sQuery(id+"F0.wireOp",EDGE,"E29.top"),sQuery(id+"F0.wireOp",EDGE,"E29.left"),sQuery(id+"F0.wireOp",EDGE,"E29.right"),subQ26,subQ28,subQ29,subQ25,subQ27,sQuery(id+"F0.wireOp",EDGE,"E34.top"),sQuery(id+"F0.wireOp",EDGE,"E34.left"),sQuery(id+"F0.wireOp",EDGE,"E34.right"),sQuery(id+"F0.wireOp",EDGE,"E35.trimOffspring")])],"isStart":false})});}
            var sketch = newSketch(context, id + "F15", { "sketchPlane" : qUnion([Q0])});
            skLineSegment(sketch, "E65.bottom", {"start": v(0.6, 0) * mm, "end": v(55.4, 0) * mm});
            skLineSegment(sketch, "E65.top", {"start": v(0.6, 6) * mm, "end": v(55.4, 6) * mm});
            skLineSegment(sketch, "E65.left", {"start": v(0.6, 0) * mm, "end": v(0.6, 6) * mm});
            skLineSegment(sketch, "E65.right", {"start": v(55.4, 0) * mm, "end": v(55.4, 6) * mm});
            skSolve(sketch);
        }
        {
            var Q0;
            Q0=makeQuery(id+"F15.imprint","IMPRINT",FACE,{"disambiguationData":[TD([[makeQuery(id+"F15.imprint","IMPRINT",EDGE,{"derivedFrom":sQuery(id+"F15.wireOp",EDGE,"E65.bottom")}),1.0]])]});
            extrude(context, id + "F16", {"entities" : qUnion([Q0]), "operationType" : NewBodyOperationType.REMOVE, "oppositeDirection" : true, "depth" : 25 * mm});
        }
        {
            var Q0;
            Q0=makeQuery(id+"F1.opExtrude","SWEPT_EDGE",EDGE,{"disambiguationData":[OSD([sQuery(id+"F0.wireOp",EDGE,"E34.top"),sQuery(id+"F0.wireOp",EDGE,"E34.right")])]});
            var Q1;
            Q1=makeQuery(id+"F1.opExtrude","SWEPT_EDGE",EDGE,{"disambiguationData":[OSD([sQuery(id+"F0.wireOp",EDGE,"E34.top"),sQuery(id+"F0.wireOp",EDGE,"E34.left")])]});
            fillet(context, id + "F17", {"entities" : qUnion([Q0, Q1]), "radius" : 6 * mm, "tangentPropagation" : true, "allowEdgeOverflow" : false});
        }
        {
            var Q0;
            Q0=makeQuery(id+"F1.opExtrude","SWEPT_EDGE",EDGE,{"disambiguationData":[OSD([sQuery(id+"F0.wireOp",EDGE,"E6.bottom"),sQuery(id+"F0.wireOp",EDGE,"E34.right")])]});
            var Q1;
            Q1=makeQuery(id+"F1.opExtrude","SWEPT_EDGE",EDGE,{"disambiguationData":[OSD([sQuery(id+"F0.wireOp",EDGE,"E34.left"),sQuery(id+"F0.wireOp",EDGE,"E35.trimOffspring")])]});
            chamfer(context, id + "F18", {"entities" : qUnion([Q0, Q1]), "width" : 16 * mm, "tangentPropagation" : true});
        }
        {
            var Q0;
            Q0=makeQuery(id+"F1.opExtrude","SWEPT_FACE",FACE,{"disambiguationData":[OSD([sQuery(id+"F0.wireOp",EDGE,"E21.right"),sQuery(id+"F0.wireOp",EDGE,"E22.left")])]});
            var sketch = newSketch(context, id + "F19", { "sketchPlane" : qUnion([Q0])});
            skLineSegment(sketch, "E66", {"start": v(-87, 0.5) * mm, "end": v(-86.65, 0.15) * mm});
            skLineSegment(sketch, "E67", {"start": v(-86.65, 0.15) * mm, "end": v(-86.35, 0.15) * mm});
            skLineSegment(sketch, "E68", {"start": v(-86.35, 0.15) * mm, "end": v(-86, 0.5) * mm});
            skLineSegment(sketch, "E69", {"start": v(-86, 0.5) * mm, "end": v(-87, 0.5) * mm});
            skSolve(sketch);
        }
        {
            var Q0;
            Q0 = qSketchRegion(id + "F19", true);
            extrude(context, id + "F20", {"entities" : qUnion([Q0]), "operationType" : NewBodyOperationType.REMOVE, "endBound" : BoundingType.UP_TO_NEXT, "oppositeDirection" : true, "depth" : 25 * mm});
        }
        {
            var Q0;
            Q0=qCreatedBy(makeId("Top.planeOp"),FACE);
            var sketch = newSketch(context, id + "F21", { "sketchPlane" : qUnion([Q0])});
            skLineSegment(sketch, "E70", {"start": v(51.9, 37.43) * mm, "end": v(66.9, 37.43) * mm});
            skLineSegment(sketch, "E71", {"start": v(66.9, 37.43) * mm, "end": v(66.9, 44.43) * mm});
            skLineSegment(sketch, "E72", {"start": v(51.9, 37.43) * mm, "end": v(51.9, 44.43) * mm});
            skArc(sketch, "E73", {"start": v(66.9, 44.43) * mm, "mid": v(59.4, 51.93) * mm, "end": v(51.9, 44.43) * mm});
            skSolve(sketch);
        }
        {
            var Q0;
            Q0 = qSketchRegion(id + "F21", true);
            extrude(context, id + "F22", {"entities" : qUnion([Q0]), "depth" : 0.5 * mm});
        }
        {
            var Q0;
            {var subQ1=sQuery(id+"F0.wireOp",EDGE,"E22.left");var subQ2=sQuery(id+"F0.wireOp",EDGE,"E21.right");var subQ4=sQuery(id+"F0.wireOp",EDGE,"E31.right");var subQ5=sQuery(id+"F0.wireOp",EDGE,"E30.right");var subQ7=sQuery(id+"F0.wireOp",EDGE,"E31.left");var subQ8=sQuery(id+"F0.wireOp",EDGE,"E30.left");var subQ10=sQuery(id+"F0.wireOp",EDGE,"E22.right");var subQ11=sQuery(id+"F0.wireOp",EDGE,"E21.left");var subQ13=makeQuery(id+"F4.opExtrude","SWEPT_FACE",FACE,{"disambiguationData":[OSD([sQuery(id+"F3.wireOp",EDGE,"E37")])]});var subQ14=sQuery(id+"F0.wireOp",EDGE,"E6.bottom");var subQ15=sQuery(id+"F0.wireOp",EDGE,"E5.bottom");var subQ16=sQuery(id+"F0.wireOp",EDGE,"E4.bottom");var subQ17=sQuery(id+"F0.wireOp",EDGE,"E3.bottom");var subQ18=sQuery(id+"F0.wireOp",EDGE,"E2.bottom");var subQ19=sQuery(id+"F0.wireOp",EDGE,"E1.bottom");var subQ21=sQuery(id+"F0.wireOp",EDGE,"E2.top");var subQ22=sQuery(id+"F0.wireOp",EDGE,"E1.top");var subQ24=sQuery(id+"F0.wireOp",EDGE,"E18.MirrorCS");var subQ25=sQuery(id+"F0.wireOp",EDGE,"E13.MirrorCS");var subQ26=sQuery(id+"F0.wireOp",EDGE,"E12.MirrorCS");var subQ27=sQuery(id+"F0.wireOp",EDGE,"E11.MirrorCS");var subQ29=sQuery(id+"F0.wireOp",EDGE,"E16.MirrorCS");var subQ30=sQuery(id+"F0.wireOp",EDGE,"E15.MirrorCS");var subQ36=sQuery(id+"F0.wireOp",EDGE,"E26.top");var subQ37=sQuery(id+"F0.wireOp",EDGE,"E26.bottom");var subQ38=sQuery(id+"F0.wireOp",EDGE,"E24.left");var subQ39=sQuery(id+"F0.wireOp",EDGE,"E26.right");var subQ40=sQuery(id+"F0.wireOp",EDGE,"E24.right");var subQ41=sQuery(id+"F0.wireOp",EDGE,"E27.bottom");var subQ42=sQuery(id+"F0.wireOp",EDGE,"E27.top");var subQ43=sQuery(id+"F0.wireOp",EDGE,"E31.top");var subQ44=sQuery(id+"F0.wireOp",EDGE,"E24.top");var subQ45=sQuery(id+"F0.wireOp",EDGE,"E27.right");Q0=makeQuery(id+"F20.boolean.opBoolean","SPLIT",FACE,{"disambiguationData":[TD([makeQuery(id+"F4.boolean.opBoolean","COPY",FACE,{"derivedFrom":subQ13})])],"derivedFrom":makeQuery(id+"F4.boolean.opBoolean","SPLIT",FACE,{"disambiguationData":[TD([makeQuery(id+"F1.opExtrude","SWEPT_FACE",FACE,{"disambiguationData":[OSD([subQ38])]})])],"derivedFrom":makeQuery(id+"F1.opExtrude","CAP_FACE",FACE,{"disambiguationData":[OSD([subQ19,subQ22,subQ18,subQ21,subQ17,subQ16,sQuery(id+"F0.wireOp",EDGE,"E4.top"),subQ15,sQuery(id+"F0.wireOp",EDGE,"E5.top"),subQ14,subQ27,subQ26,subQ25,subQ30,subQ29,sQuery(id+"F0.wireOp",EDGE,"E17.MirrorCS"),subQ24,sQuery(id+"F0.wireOp",EDGE,"E19.MirrorCS"),sQuery(id+"F0.wireOp",EDGE,"E20.bottom"),sQuery(id+"F0.wireOp",EDGE,"E20.top"),sQuery(id+"F0.wireOp",EDGE,"E20.right"),subQ11,subQ2,subQ1,subQ10,subQ44,subQ38,subQ40,sQuery(id+"F0.wireOp",EDGE,"E25.top"),sQuery(id+"F0.wireOp",EDGE,"E25.left"),sQuery(id+"F0.wireOp",EDGE,"E25.right"),subQ37,subQ36,subQ39,subQ41,subQ42,subQ45,sQuery(id+"F0.wireOp",EDGE,"E28.top"),sQuery(id+"F0.wireOp",EDGE,"E28.left"),sQuery(id+"F0.wireOp",EDGE,"E28.right"),sQuery(id+"F0.wireOp",EDGE,"E29.top"),sQuery(id+"F0.wireOp",EDGE,"E29.left"),sQuery(id+"F0.wireOp",EDGE,"E29.right"),subQ8,subQ5,subQ43,subQ7,subQ4,sQuery(id+"F0.wireOp",EDGE,"E34.top"),sQuery(id+"F0.wireOp",EDGE,"E34.left"),sQuery(id+"F0.wireOp",EDGE,"E34.right"),sQuery(id+"F0.wireOp",EDGE,"E35.trimOffspring")])],"isStart":false})})});}
            var sketch = newSketch(context, id + "F23", { "sketchPlane" : qUnion([Q0])});
            skLineSegment(sketch, "E74.bottom", {"start": v(46, -46.83) * mm, "end": v(10, -46.83) * mm});
            skLineSegment(sketch, "E74.left", {"start": v(54, -38.83) * mm, "end": v(54, 15.17) * mm});
            skLineSegment(sketch, "E74.right", {"start": v(2, -38.83) * mm, "end": v(2, 15.17) * mm});
            skLineSegment(sketch, "E75", {"start": v(2, 15.17) * mm, "end": v(21.33, 34.5) * mm});
            skLineSegment(sketch, "E76", {"start": v(54, 15.17) * mm, "end": v(34.67, 34.5) * mm});
            skLineSegment(sketch, "E77", {"start": v(34.67, 34.5) * mm, "end": v(21.33, 34.5) * mm});
            skPoint(sketch, "E78.visualSharp", {"position": v(2, -46.83) * mm});
            skArc(sketch, "E78.filletArc", {"start": v(2, -38.83) * mm, "mid": v(4.34, -44.49) * mm, "end": v(10, -46.83) * mm});
            skPoint(sketch, "E79.visualSharp", {"position": v(54, -46.83) * mm});
            skArc(sketch, "E79.filletArc", {"start": v(46, -46.83) * mm, "mid": v(51.66, -44.49) * mm, "end": v(54, -38.83) * mm});
            skSolve(sketch);
        }
        {
            var Q0;
            Q0=makeQuery(id+"F1.opExtrude","CAP_FACE",FACE,{"disambiguationData":[OSD([sQuery(id+"F0.wireOp",EDGE,"E1.bottom"),sQuery(id+"F0.wireOp",EDGE,"E1.top"),sQuery(id+"F0.wireOp",EDGE,"E2.bottom"),sQuery(id+"F0.wireOp",EDGE,"E2.top"),sQuery(id+"F0.wireOp",EDGE,"E3.bottom"),sQuery(id+"F0.wireOp",EDGE,"E4.bottom"),sQuery(id+"F0.wireOp",EDGE,"E4.top"),sQuery(id+"F0.wireOp",EDGE,"E5.bottom"),sQuery(id+"F0.wireOp",EDGE,"E5.top"),sQuery(id+"F0.wireOp",EDGE,"E6.bottom"),sQuery(id+"F0.wireOp",EDGE,"E11.MirrorCS"),sQuery(id+"F0.wireOp",EDGE,"E12.MirrorCS"),sQuery(id+"F0.wireOp",EDGE,"E13.MirrorCS"),sQuery(id+"F0.wireOp",EDGE,"E15.MirrorCS"),sQuery(id+"F0.wireOp",EDGE,"E16.MirrorCS"),sQuery(id+"F0.wireOp",EDGE,"E17.MirrorCS"),sQuery(id+"F0.wireOp",EDGE,"E18.MirrorCS"),sQuery(id+"F0.wireOp",EDGE,"E19.MirrorCS"),sQuery(id+"F0.wireOp",EDGE,"E20.bottom"),sQuery(id+"F0.wireOp",EDGE,"E20.top"),sQuery(id+"F0.wireOp",EDGE,"E20.right"),sQuery(id+"F0.wireOp",EDGE,"E21.left"),sQuery(id+"F0.wireOp",EDGE,"E21.right"),sQuery(id+"F0.wireOp",EDGE,"E22.left"),sQuery(id+"F0.wireOp",EDGE,"E22.right"),sQuery(id+"F0.wireOp",EDGE,"E24.top"),sQuery(id+"F0.wireOp",EDGE,"E24.left"),sQuery(id+"F0.wireOp",EDGE,"E24.right"),sQuery(id+"F0.wireOp",EDGE,"E25.top"),sQuery(id+"F0.wireOp",EDGE,"E25.left"),sQuery(id+"F0.wireOp",EDGE,"E25.right"),sQuery(id+"F0.wireOp",EDGE,"E26.bottom"),sQuery(id+"F0.wireOp",EDGE,"E26.top"),sQuery(id+"F0.wireOp",EDGE,"E26.right"),sQuery(id+"F0.wireOp",EDGE,"E27.bottom"),sQuery(id+"F0.wireOp",EDGE,"E27.top"),sQuery(id+"F0.wireOp",EDGE,"E27.right"),sQuery(id+"F0.wireOp",EDGE,"E28.top"),sQuery(id+"F0.wireOp",EDGE,"E28.left"),sQuery(id+"F0.wireOp",EDGE,"E28.right"),sQuery(id+"F0.wireOp",EDGE,"E29.top"),sQuery(id+"F0.wireOp",EDGE,"E29.left"),sQuery(id+"F0.wireOp",EDGE,"E29.right"),sQuery(id+"F0.wireOp",EDGE,"E30.left"),sQuery(id+"F0.wireOp",EDGE,"E30.right"),sQuery(id+"F0.wireOp",EDGE,"E31.top"),sQuery(id+"F0.wireOp",EDGE,"E31.left"),sQuery(id+"F0.wireOp",EDGE,"E31.right"),sQuery(id+"F0.wireOp",EDGE,"E34.top"),sQuery(id+"F0.wireOp",EDGE,"E34.left"),sQuery(id+"F0.wireOp",EDGE,"E34.right"),sQuery(id+"F0.wireOp",EDGE,"E35.trimOffspring")])],"isStart":true});
            var sketch = newSketch(context, id + "F24", { "sketchPlane" : qUnion([Q0])});
            skLineSegment(sketch, "E80.0", {"start": v(54, 38.83) * mm, "end": v(54, -15.17) * mm});
            skLineSegment(sketch, "E80.1", {"start": v(54, -15.17) * mm, "end": v(34.67, -34.5) * mm});
            skLineSegment(sketch, "E80.2", {"start": v(34.67, -34.5) * mm, "end": v(21.33, -34.5) * mm});
            skLineSegment(sketch, "E80.3", {"start": v(2, -15.17) * mm, "end": v(21.33, -34.5) * mm});
            skLineSegment(sketch, "E80.4", {"start": v(2, 38.83) * mm, "end": v(2, -15.17) * mm});
            skArc(sketch, "E80.5", {"start": v(46, 46.83) * mm, "mid": v(51.66, 44.49) * mm, "end": v(54, 38.83) * mm});
            skLineSegment(sketch, "E80.6", {"start": v(46, 46.83) * mm, "end": v(10, 46.83) * mm});
            skArc(sketch, "E80.7", {"start": v(2, 38.83) * mm, "mid": v(4.34, 44.49) * mm, "end": v(10, 46.83) * mm});
            skSolve(sketch);
        }
        {
            var Q0;
            Q0 = qSketchRegion(id + "F24", true);
            extrude(context, id + "F25", {"entities" : qUnion([Q0]), "operationType" : NewBodyOperationType.REMOVE, "oppositeDirection" : true, "depth" : 0.25 * mm});
        }
    });
